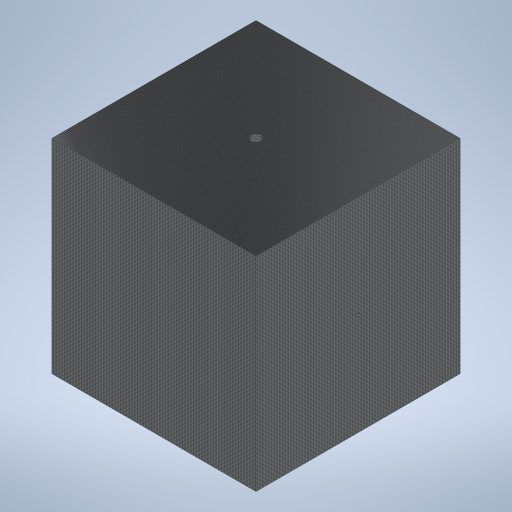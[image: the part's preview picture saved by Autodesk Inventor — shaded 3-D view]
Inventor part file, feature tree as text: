
AUTODESK INVENTOR PART (.ipt)
format: ipt  version: 2024 (Build 280153000, 153)  size: 412,160 bytes
history: native  units: mm
features: extrude x5, sketch x1
ambient origin geometry x8: Origin, YZ Plane, XZ Plane, XY Plane, X Axis, Y Axis, Z Axis, Center Point
bodies: Solid1 (feature_tree)
feature tree (6):
  extrude  "Extrusion1"  Depth=300.0mm
  extrude  "Extrusion3"  Depth=300.0mm TaperAngle=0.0deg
  extrude  "Extrusion5"  Depth=10.0mm
  extrude  "Extrusion7"  Depth=20.0mm
  extrude  "Extrusion8"  Depth=30.0mm
  sketch  "Sketch8"  dims[d0=300.0mm d1=300.0mm d2=300.0mm d3=0.0mm d10=10.0mm d11=20.0mm d12=30.0mm d13=30.0mm d14=10.0mm d15=0.0mm d22=10.0mm d23=10.0mm d24=10.0mm d25=10.0mm d26=290.0mm d27=0.0mm d37=5.0mm d38=150.0mm d39=150.0mm d40=10.0mm d41=0.0mm d42=15.0mm d43=150.0mm d44=150.0mm d45=0.0mm d46=0.0mm]
